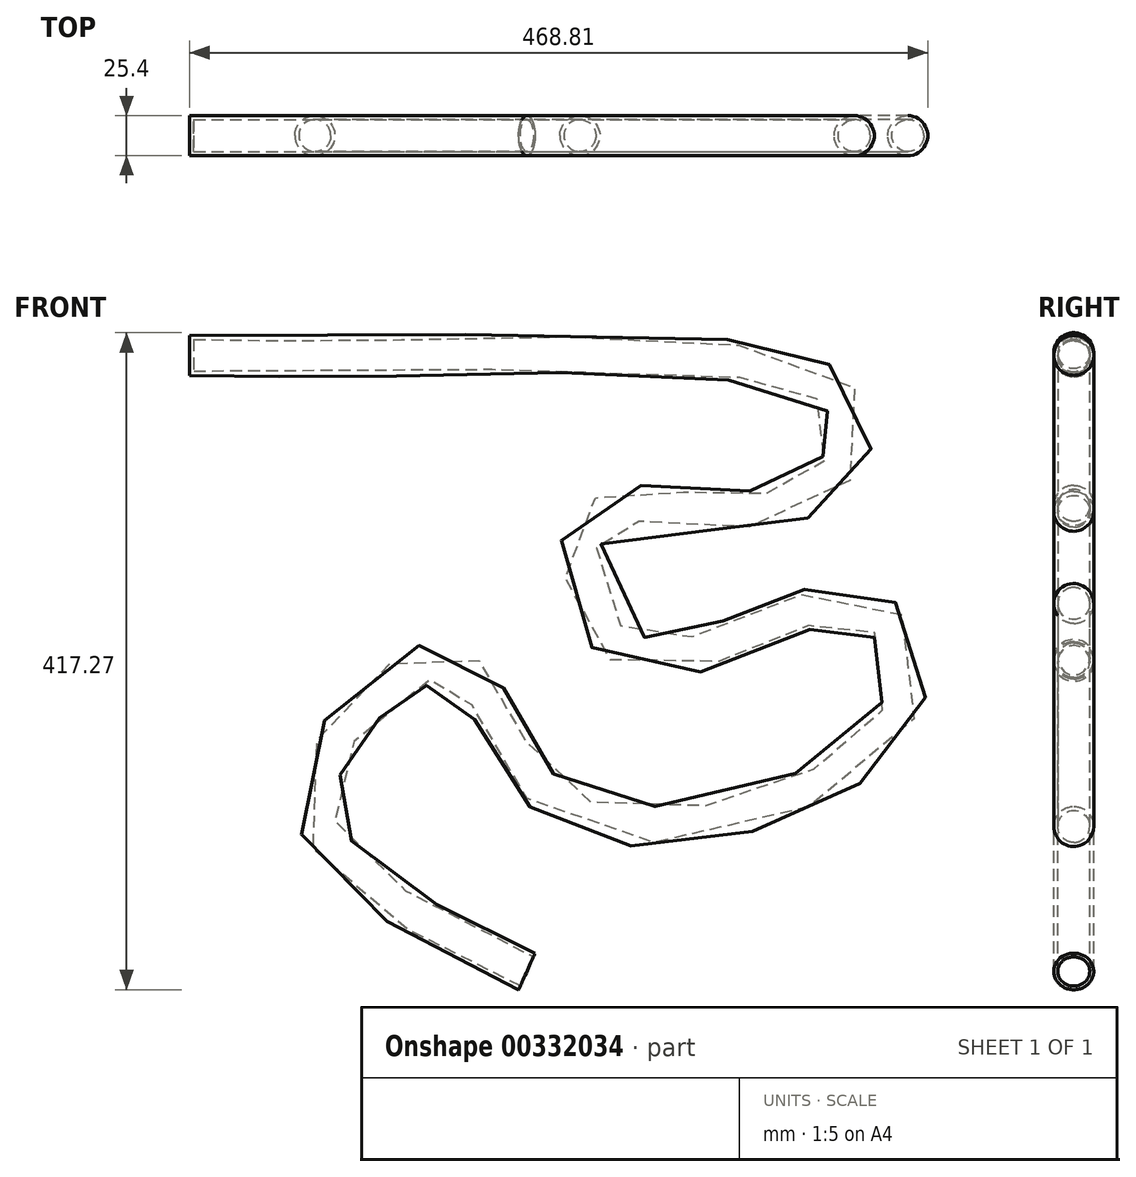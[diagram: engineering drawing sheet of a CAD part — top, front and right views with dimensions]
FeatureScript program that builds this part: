
annotation { "Feature Type Name" : "Feature", "Feature Type Description" : "" }
export const myFeature = defineFeature(function(context is Context, id is Id, definition is map)
    precondition{}
    {
        {
            var Q0;
            Q0=qCreatedBy(makeId("Right.planeOp"),FACE);
            var sketch = newSketch(context, id + "F0", { "sketchPlane" : qUnion([Q0])});
            skCircle(sketch, "E0", {"center": v(0, 0) * mm, "radius": 12.7 * mm});
            skSolve(sketch);
        }
        {
            var Q0;
            Q0=qCreatedBy(makeId("Front.planeOp"),FACE);
            var sketch = newSketch(context, id + "F1", { "sketchPlane" : qUnion([Q0])});
            skFitSpline(sketch, "E1", {"points": [v(0, 0) * mm, v(146.71, 0) * mm, v(417.74, -31.07) * mm, v(378.26, -95.22) * mm, v(254.89, -105.1) * mm, v(282.03, -190.22) * mm, v(421.44, -158.14) * mm, v(448.58, -230.93) * mm, v(236.38, -286.44) * mm, v(166.06, -195.15) * mm, v(79.7, -277.8) * mm, v(214.18, -391.3) * mm], "startDerivative": vector(1234.1, -24.26) * mm, "endDerivative": vector(2020.36, -952.46) * mm});
            skSolve(sketch);
        }
        {
            var Q0;
            Q0=makeQuery(id+"F0.imprint","IMPRINT",FACE,{"disambiguationData":[TD([[makeQuery(id+"F0.imprint","IMPRINT",EDGE,{"derivedFrom":sQuery(id+"F0.wireOp",EDGE,"E0")}),1.0]])]});
            var Q1;
            Q1=sQuery(id+"F1.wireOp",EDGE,"E1");
            sweep(context, id + "F2", {"profiles" : qUnion([Q0]), "path" : qUnion([Q1])});
        }
        {
            var Q0;
            Q0=makeQuery(id+"F2.opSweep","CAP_FACE",FACE,{"disambiguationData":[OSD([sQuery(id+"F0.wireOp",EDGE,"E0"),sQuery(id+"F1.wireOp",VERTEX,"E1.end")])],"isStart":false});
            shell(context, id + "F3", {"entities" : qUnion([Q0]), "thickness" : 2.54 * mm});
        }
    });
